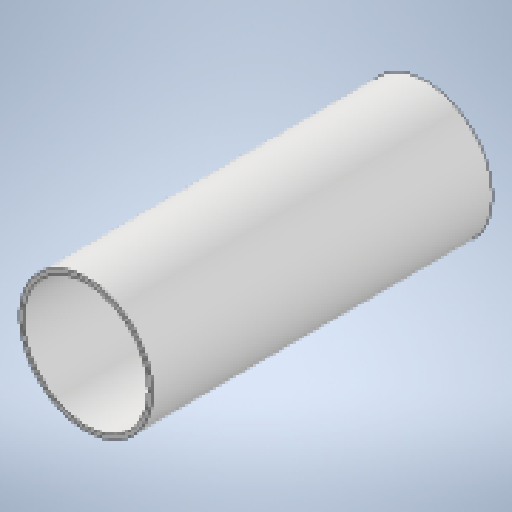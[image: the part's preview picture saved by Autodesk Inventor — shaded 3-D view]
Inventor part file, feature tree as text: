
AUTODESK INVENTOR PART (.ipt)
format: ipt  version: 2025.1 (Build 291241020, 241B)  size: 142,848 bytes
history: native  units: mm
features: extrude x1, sketch x1
ambient origin geometry x8: Origin, YZ Plane, XZ Plane, XY Plane, X Axis, Y Axis, Z Axis, Center Point
bodies: Solid1 (feature_tree)
feature tree (2):
  extrude  "Extrusion1"  Depth=230.0mm
  sketch  "Sketch1"  dims[d0=90.0mm d1=3.0mm d2=230.0mm d3=0.0mm]
